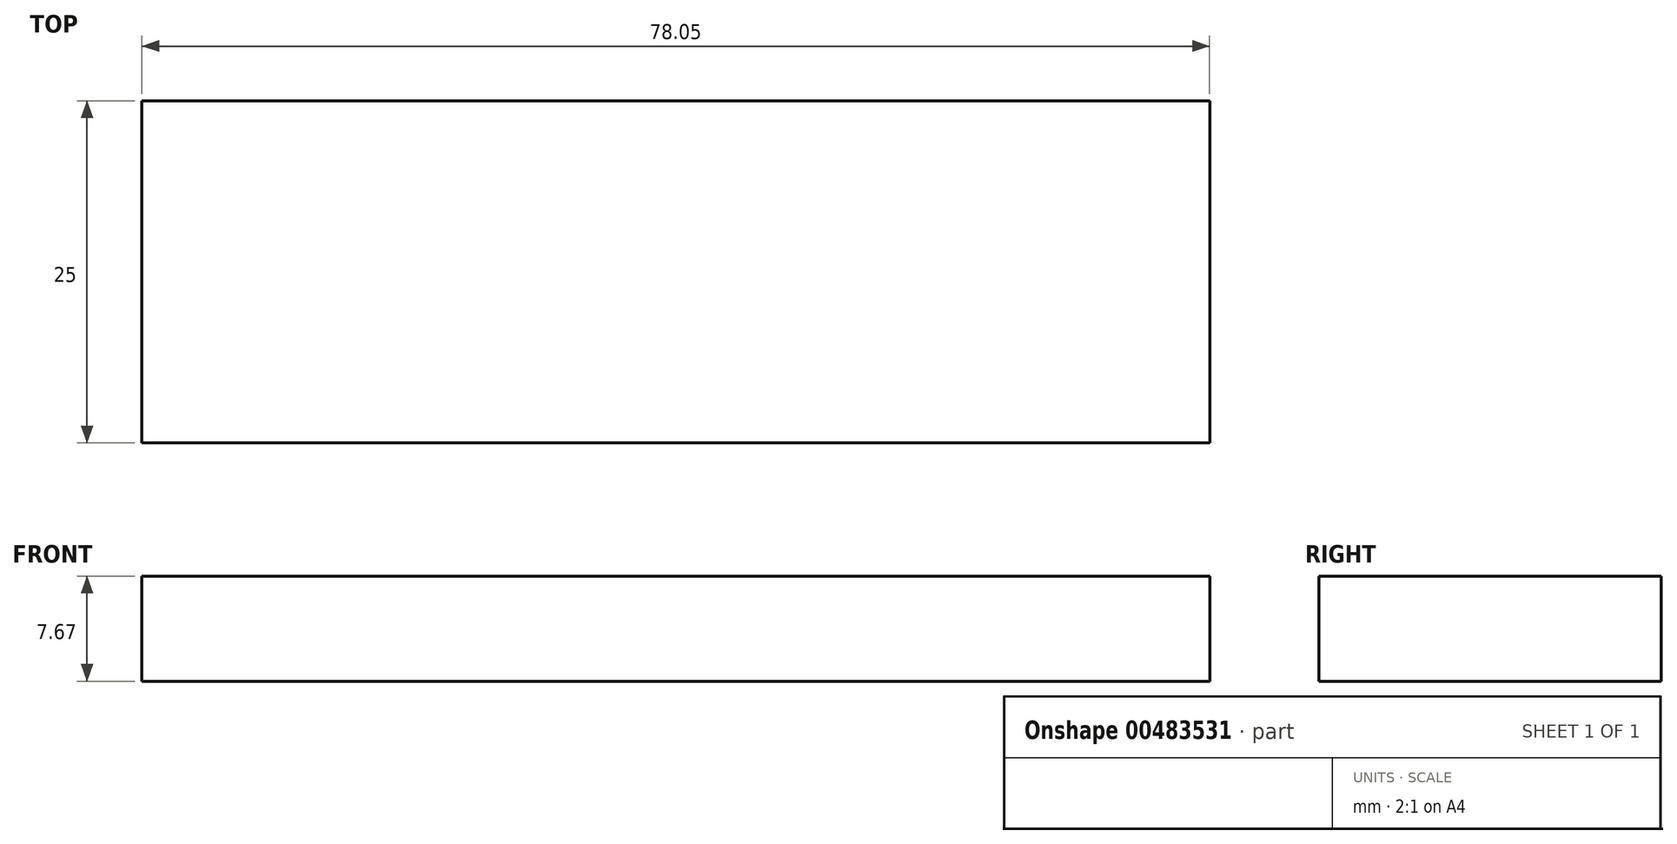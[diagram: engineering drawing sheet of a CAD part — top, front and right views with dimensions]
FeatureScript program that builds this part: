
annotation { "Feature Type Name" : "Feature", "Feature Type Description" : "" }
export const myFeature = defineFeature(function(context is Context, id is Id, definition is map)
    precondition{}
    {
        {
            var Q0;
            Q0=qCreatedBy(makeId("Front.planeOp"),FACE);
            var sketch = newSketch(context, id + "F0", { "sketchPlane" : qUnion([Q0])});
            skLineSegment(sketch, "E0.bottom", {"start": v(-35.5, 0) * mm, "end": v(42.56, 0) * mm});
            skLineSegment(sketch, "E0.top", {"start": v(-35.5, 7.67) * mm, "end": v(42.56, 7.67) * mm});
            skLineSegment(sketch, "E0.left", {"start": v(-35.5, 0) * mm, "end": v(-35.5, 7.67) * mm});
            skLineSegment(sketch, "E0.right", {"start": v(42.56, 0) * mm, "end": v(42.56, 7.67) * mm});
            skSolve(sketch);
        }
        {
            var Q0;
            Q0=makeQuery(id+"F0.imprint","IMPRINT",FACE,{"disambiguationData":[TD([[makeQuery(id+"F0.imprint","IMPRINT",EDGE,{"derivedFrom":sQuery(id+"F0.wireOp",EDGE,"E0.bottom")}),1.0]])]});
            extrude(context, id + "F1", {"entities" : qUnion([Q0]), "depth" : 25 * mm});
        }
    });
